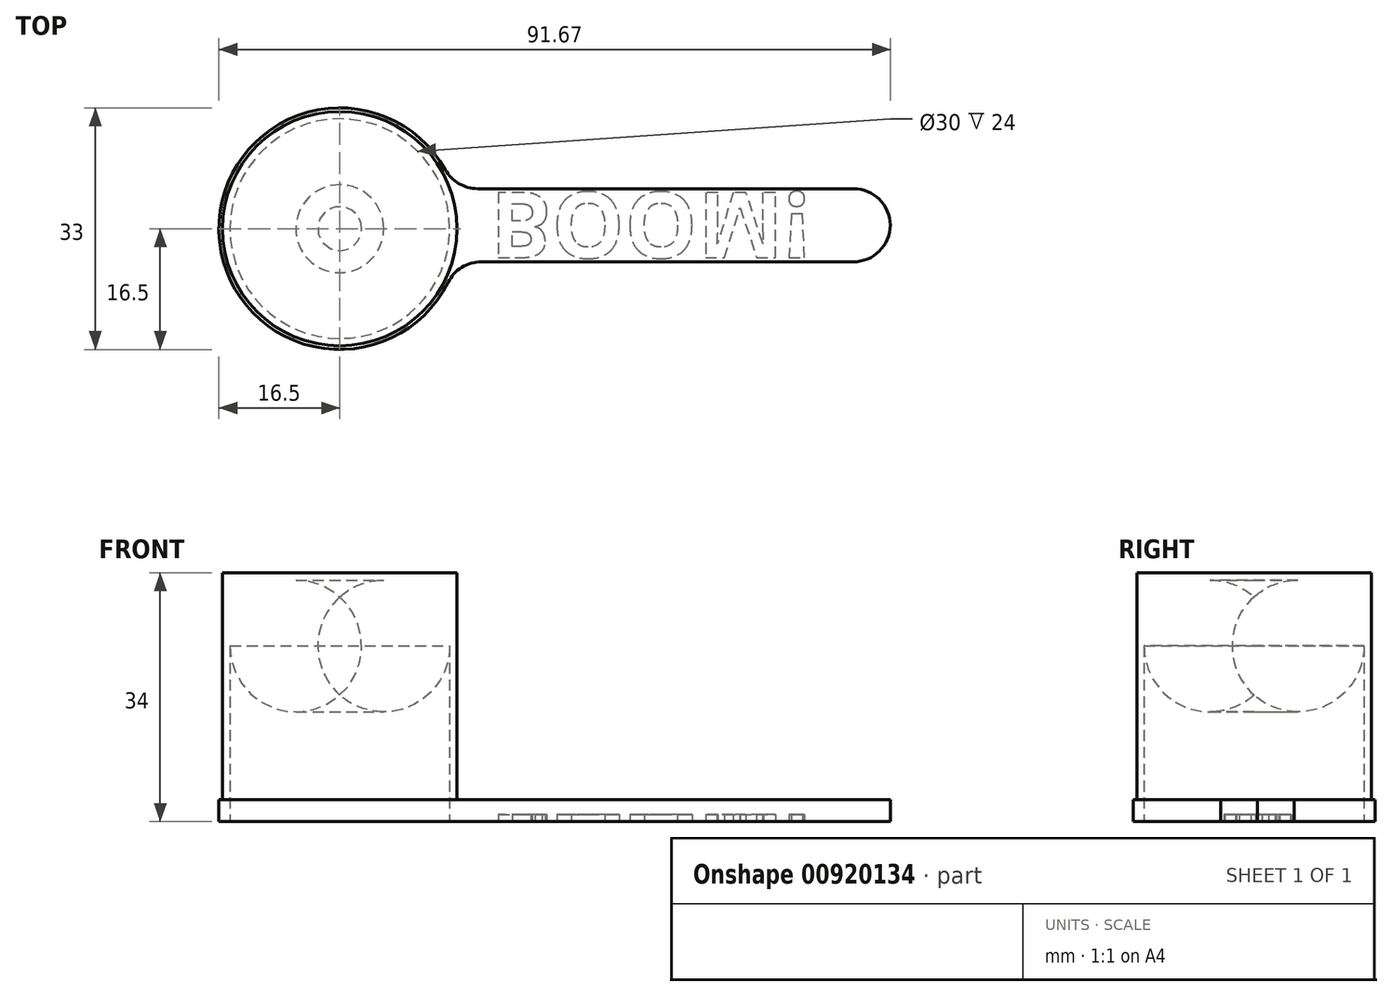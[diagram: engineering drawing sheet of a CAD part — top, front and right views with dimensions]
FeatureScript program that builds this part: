
annotation { "Feature Type Name" : "Feature", "Feature Type Description" : "" }
export const myFeature = defineFeature(function(context is Context, id is Id, definition is map)
    precondition{}
    {
        {
            var Q0;
            Q0=qCreatedBy(makeId("Top.planeOp"),FACE);
            var sketch = newSketch(context, id + "F0", { "sketchPlane" : qUnion([Q0])});
            skCircle(sketch, "E0", {"center": v(0, 0) * mm, "radius": 16.5 * mm});
            skLineSegment(sketch, "E1.left", {"start": v(75.17, 5.47) * mm, "end": v(75.17, -4.69) * mm});
            skLineSegment(sketch, "E2.bottom", {"start": v(75.17, 5.47) * mm, "end": v(15.57, 5.47) * mm});
            skLineSegment(sketch, "E2.top", {"start": v(75.17, -4.53) * mm, "end": v(15.87, -4.53) * mm});
            skLineSegment(sketch, "E2.left", {"start": v(75.17, 5.47) * mm, "end": v(75.17, -4.53) * mm});
            skSolve(sketch);
        }
        {
            var Q0;
            Q0 = qSketchRegion(id + "F0", true);
            extrude(context, id + "F1", {"entities" : qUnion([Q0]), "depth" : 3 * mm, "offsetDistance" : 25.4 * mm});
        }
        {
            var Q0;
            Q0=makeQuery(id+"F1.opExtrude","CAP_FACE",FACE,{"disambiguationData":[OSD([sQuery(id+"F0.wireOp",EDGE,"E0"),sQuery(id+"F0.wireOp",EDGE,"E2.bottom"),sQuery(id+"F0.wireOp",EDGE,"E2.top"),sQuery(id+"F0.wireOp",EDGE,"E2.left")])],"isStart":false});
            var sketch = newSketch(context, id + "F2", { "sketchPlane" : qUnion([Q0])});
            skSolve(sketch);
        }
        {
            var Q0;
            Q0=makeQuery(id+"F2.imprint","IMPRINT",FACE,{"disambiguationData":[TD([[makeQuery(id+"F2.imprint","IMPRINT",EDGE,{"derivedFrom":makeQuery(id+"F1.opExtrude","CAP_EDGE",EDGE,{"disambiguationData":[OSD([sQuery(id+"F0.wireOp",EDGE,"E0")])],"isStart":false})}),1.0]])]});
            var sketch = newSketch(context, id + "F3", { "sketchPlane" : qUnion([Q0])});
            skCircle(sketch, "E3", {"center": v(0, 0) * mm, "radius": 16 * mm});
            skSolve(sketch);
        }
        {
            var Q0;
            Q0=makeQuery(id+"F3.imprint","IMPRINT",FACE,{"disambiguationData":[TD([[makeQuery(id+"F3.imprint","IMPRINT",EDGE,{"derivedFrom":sQuery(id+"F3.wireOp",EDGE,"E3")}),1.0]])]});
            extrude(context, id + "F4", {"entities" : qUnion([Q0]), "operationType" : NewBodyOperationType.ADD, "depth" : 31 * mm, "offsetDistance" : 25.4 * mm});
        }
        {
            var Q0;
            Q0=makeQuery(id+"F1.opExtrude","CAP_FACE",FACE,{"disambiguationData":[OSD([sQuery(id+"F0.wireOp",EDGE,"E0"),sQuery(id+"F0.wireOp",EDGE,"E2.bottom"),sQuery(id+"F0.wireOp",EDGE,"E2.top"),sQuery(id+"F0.wireOp",EDGE,"E2.left")])],"isStart":true});
            var sketch = newSketch(context, id + "F5", { "sketchPlane" : qUnion([Q0])});
            skCircle(sketch, "E4", {"center": v(0, 0) * mm, "radius": 15 * mm});
            skSolve(sketch);
        }
        {
            var Q0;
            Q0 = qSketchRegion(id + "F5", true);
            extrude(context, id + "F6", {"entities" : qUnion([Q0]), "operationType" : NewBodyOperationType.REMOVE, "oppositeDirection" : true, "depth" : 33 * mm, "offsetDistance" : 25.4 * mm});
        }
        {
            var Q0;
            Q0=makeQuery(id+"F1.opExtrude","SWEPT_EDGE",EDGE,{"disambiguationData":[OSD([sQuery(id+"F0.wireOp",EDGE,"E0"),sQuery(id+"F0.wireOp",EDGE,"E2.bottom")])]});
            var Q1;
            Q1=makeQuery(id+"F1.opExtrude","SWEPT_EDGE",EDGE,{"disambiguationData":[OSD([sQuery(id+"F0.wireOp",EDGE,"E2.bottom"),sQuery(id+"F0.wireOp",EDGE,"E2.left")])]});
            var Q2;
            Q2=makeQuery(id+"F1.opExtrude","SWEPT_EDGE",EDGE,{"disambiguationData":[OSD([sQuery(id+"F0.wireOp",EDGE,"E2.top"),sQuery(id+"F0.wireOp",EDGE,"E2.left")])]});
            var Q3;
            Q3=makeQuery(id+"F1.opExtrude","SWEPT_EDGE",EDGE,{"disambiguationData":[OSD([sQuery(id+"F0.wireOp",EDGE,"E0"),sQuery(id+"F0.wireOp",EDGE,"E2.top")])]});
            fillet(context, id + "F7", {"entities" : qUnion([Q0, Q1, Q2, Q3]), "radius" : 5.08 * mm, "tangentPropagation" : true, "allowEdgeOverflow" : false});
        }
        {
            var Q0;
            Q0=makeQuery(id+"F6.boolean.opBoolean","COPY",EDGE,{"derivedFrom":makeQuery(id+"F6.opExtrude","CAP_EDGE",EDGE,{"disambiguationData":[OSD([sQuery(id+"F5.wireOp",EDGE,"E4")])],"isStart":false})});
            fillet(context, id + "F8", {"entities" : qUnion([Q0]), "radius" : 9 * mm, "tangentPropagation" : true, "allowEdgeOverflow" : false});
        }
        {
            var Q0;
            Q0=makeQuery(id+"F1.opExtrude","CAP_FACE",FACE,{"disambiguationData":[OSD([sQuery(id+"F0.wireOp",EDGE,"E0"),sQuery(id+"F0.wireOp",EDGE,"E2.bottom"),sQuery(id+"F0.wireOp",EDGE,"E2.top"),sQuery(id+"F0.wireOp",EDGE,"E2.left")])],"isStart":true});
            var sketch = newSketch(context, id + "F9", { "sketchPlane" : qUnion([Q0])});
            skText(sketch, "E5", { "text": "BOOM!", "fontName": "OpenSans-Bold.ttf"});
            const initialGuessF9  = {"E5": [0.02052, -0.00496, 1, 0, 0.009]};
            skSetInitialGuess(sketch, initialGuessF9);
            skSolve(sketch);
        }
        {
            var Q0;
            Q0=makeQuery(id+"F9.imprint","IMPRINT",FACE,{"disambiguationData":[TD([[makeQuery(id+"F9.imprint","IMPRINT",EDGE,{"derivedFrom":sQuery(id+"F9.wireOp",EDGE,"E5.sketch_text.stroke-0")}),-1.0]])]});
            var Q1;
            Q1=makeQuery(id+"F9.imprint","IMPRINT",FACE,{"disambiguationData":[TD([[makeQuery(id+"F9.imprint","IMPRINT",EDGE,{"derivedFrom":sQuery(id+"F9.wireOp",EDGE,"E5.sketch_text.stroke-25")}),-1.0]])]});
            var Q2;
            Q2=makeQuery(id+"F9.imprint","IMPRINT",FACE,{"disambiguationData":[TD([[makeQuery(id+"F9.imprint","IMPRINT",EDGE,{"derivedFrom":sQuery(id+"F9.wireOp",EDGE,"E5.sketch_text.stroke-39")}),-1.0]])]});
            var Q3;
            Q3=makeQuery(id+"F9.imprint","IMPRINT",FACE,{"disambiguationData":[TD([[makeQuery(id+"F9.imprint","IMPRINT",EDGE,{"derivedFrom":sQuery(id+"F9.wireOp",EDGE,"E5.sketch_text.stroke-53")}),-1.0]])]});
            var Q4;
            Q4=makeQuery(id+"F9.imprint","IMPRINT",FACE,{"disambiguationData":[TD([[makeQuery(id+"F9.imprint","IMPRINT",EDGE,{"derivedFrom":sQuery(id+"F9.wireOp",EDGE,"E5.sketch_text.stroke-72")}),-1.0]])]});
            var Q5;
            Q5=makeQuery(id+"F9.imprint","IMPRINT",FACE,{"disambiguationData":[TD([[makeQuery(id+"F9.imprint","IMPRINT",EDGE,{"derivedFrom":sQuery(id+"F9.wireOp",EDGE,"E5.sketch_text.stroke-76")}),-1.0]])]});
            extrude(context, id + "F10", {"entities" : qUnion([Q0, Q1, Q2, Q3, Q4, Q5]), "operationType" : NewBodyOperationType.REMOVE, "oppositeDirection" : true, "depth" : 1 * mm, "offsetDistance" : 25.4 * mm});
        }
    });
